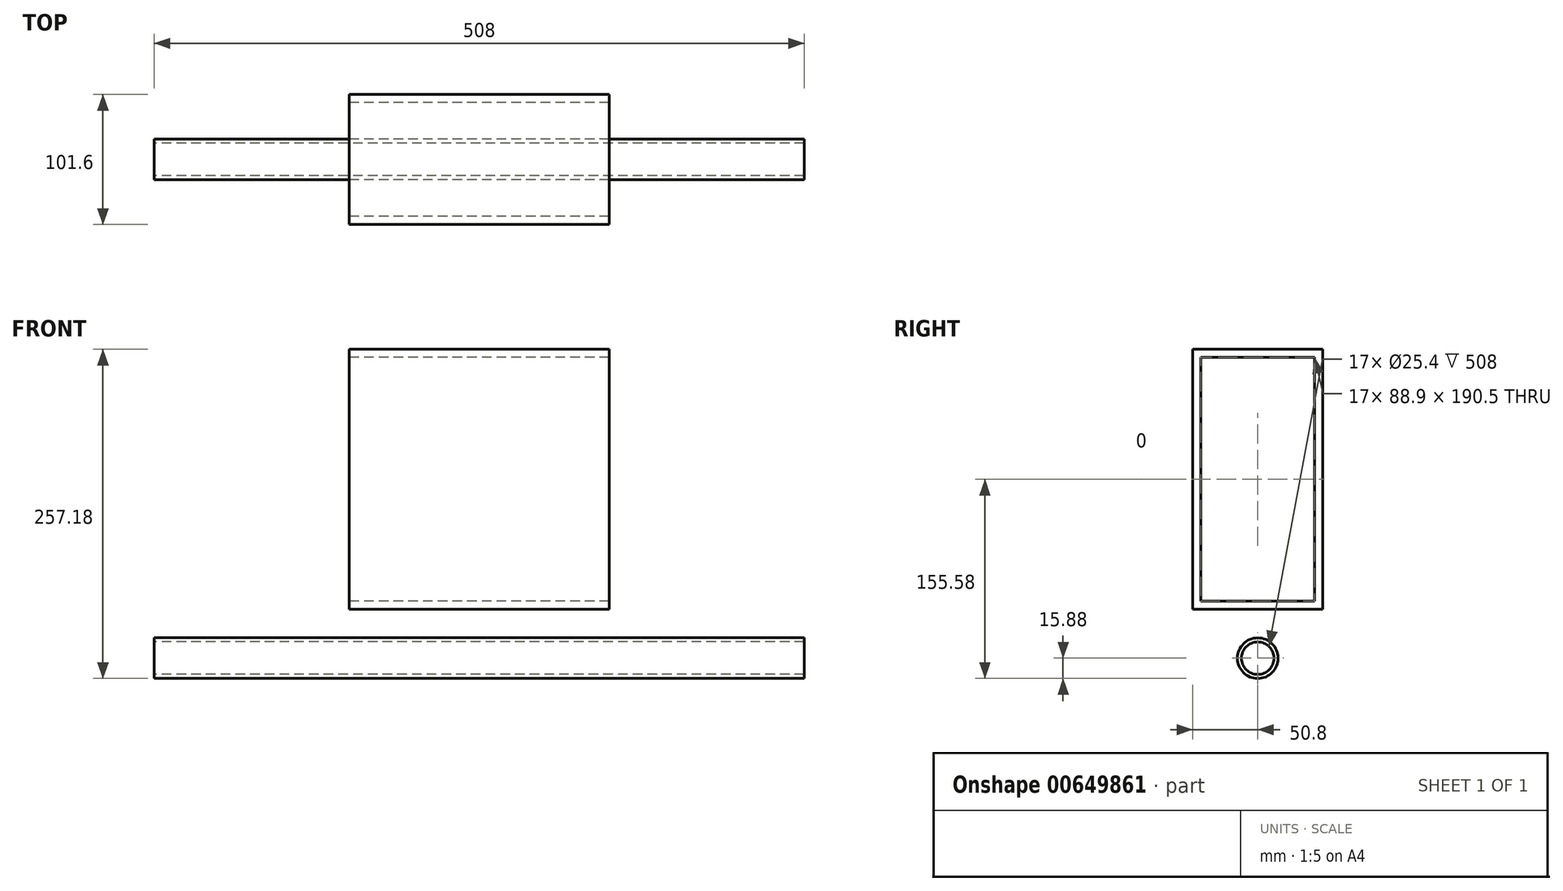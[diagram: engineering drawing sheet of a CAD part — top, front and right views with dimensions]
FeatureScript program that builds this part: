
annotation { "Feature Type Name" : "Feature", "Feature Type Description" : "" }
export const myFeature = defineFeature(function(context is Context, id is Id, definition is map)
    precondition{}
    {
        {
            var Q0;
            Q0=qCreatedBy(makeId("Right.planeOp"),FACE);
            var sketch = newSketch(context, id + "F0", { "sketchPlane" : qUnion([Q0])});
            skCircle(sketch, "E0", {"center": v(0, 0) * mm, "radius": 15.88 * mm});
            skCircle(sketch, "E1", {"center": v(0, 0) * mm, "radius": 12.7 * mm});
            skSolve(sketch);
        }
        {
            var Q0;
            Q0 = qSketchRegion(id + "F0", true);
            extrude(context, id + "F1", {"entities" : qUnion([Q0]), "depth" : 254 * mm, "offsetDistance" : 25.4 * mm, "hasSecondDirection" : true, "secondDirectionOppositeDirection" : true, "secondDirectionDepth" : 254 * mm});
        }
        {
            var Q0;
            Q0=qCreatedBy(makeId("Right.planeOp"),FACE);
            var sketch = newSketch(context, id + "F2", { "sketchPlane" : qUnion([Q0])});
            skLineSegment(sketch, "E2.bottom", {"start": v(-50.8, 241.3) * mm, "end": v(50.8, 241.3) * mm});
            skLineSegment(sketch, "E2.top", {"start": v(-50.8, 38.1) * mm, "end": v(50.8, 38.1) * mm});
            skLineSegment(sketch, "E2.left", {"start": v(-50.8, 241.3) * mm, "end": v(-50.8, 38.1) * mm});
            skLineSegment(sketch, "E2.right", {"start": v(50.8, 241.3) * mm, "end": v(50.8, 38.1) * mm});
            skLineSegment(sketch, "E3.0", {"start": v(-44.45, 234.95) * mm, "end": v(44.45, 234.95) * mm});
            skLineSegment(sketch, "E3.1", {"start": v(-44.45, 234.95) * mm, "end": v(-44.45, 44.45) * mm});
            skLineSegment(sketch, "E3.2", {"start": v(-44.45, 44.45) * mm, "end": v(44.45, 44.45) * mm});
            skLineSegment(sketch, "E3.3", {"start": v(44.45, 234.95) * mm, "end": v(44.45, 44.45) * mm});
            skSolve(sketch);
        }
        {
            var Q0;
            Q0=makeQuery(id+"F2.imprint","IMPRINT",FACE,{"disambiguationData":[TD([[makeQuery(id+"F2.imprint","IMPRINT",EDGE,{"derivedFrom":sQuery(id+"F2.wireOp",EDGE,"E2.bottom")}),-1.0]])]});
            extrude(context, id + "F3", {"entities" : qUnion([Q0]), "depth" : 101.6 * mm, "offsetDistance" : 25.4 * mm, "hasSecondDirection" : true, "secondDirectionOppositeDirection" : true, "secondDirectionDepth" : 101.6 * mm});
        }
        {
            var Q0;
            Q0=qCreatedBy(makeId("Front.planeOp"),FACE);
            var sketch = newSketch(context, id + "F4", { "sketchPlane" : qUnion([Q0])});
            skLineSegment(sketch, "E4.bottom", {"start": v(-101.6, 38.1) * mm, "end": v(101.6, 38.1) * mm});
            skLineSegment(sketch, "E4.top", {"start": v(-101.6, 0) * mm, "end": v(101.6, 0) * mm});
            skLineSegment(sketch, "E4.left", {"start": v(-101.6, 38.1) * mm, "end": v(-101.6, 0) * mm});
            skLineSegment(sketch, "E4.right", {"start": v(101.6, 38.1) * mm, "end": v(101.6, 0) * mm});
            skLineSegment(sketch, "E5.0", {"start": v(-95.25, 31.75) * mm, "end": v(-95.25, 0) * mm});
            skLineSegment(sketch, "E5.1", {"start": v(-95.25, 31.75) * mm, "end": v(95.25, 31.75) * mm});
            skLineSegment(sketch, "E5.2", {"start": v(95.25, 31.75) * mm, "end": v(95.25, 0) * mm});
            skSolve(sketch);
        }
        {
            var Q0;
            Q0=makeQuery(id+"F4.imprint","IMPRINT",FACE,{"disambiguationData":[TD([[makeQuery(id+"F4.imprint","IMPRINT",EDGE,{"derivedFrom":sQuery(id+"F4.wireOp",EDGE,"E4.bottom")}),-1.0]])]});
            extrude(context, id + "F5", {"entities" : qUnion([Q0]), "depth" : 63.5 * mm, "offsetDistance" : 25.4 * mm, "hasSecondDirection" : true, "secondDirectionOppositeDirection" : true, "secondDirectionDepth" : 63.5 * mm});
        }
        {
            var Q0;
            Q0=makeQuery(id+"F1.opExtrude","SWEPT_BODY",BODY,{"disambiguationData":[OSD([sQuery(id+"F0.wireOp",EDGE,"E0"),sQuery(id+"F0.wireOp",EDGE,"E1")])]});
            var Q1;
            Q1=makeQuery(id+"F5.opExtrude","SWEPT_BODY",BODY,{"disambiguationData":[OSD([sQuery(id+"F4.wireOp",EDGE,"E4.bottom"),sQuery(id+"F4.wireOp",EDGE,"E4.top"),sQuery(id+"F4.wireOp",EDGE,"E4.left"),sQuery(id+"F4.wireOp",EDGE,"E4.right"),sQuery(id+"F4.wireOp",EDGE,"E5.0"),sQuery(id+"F4.wireOp",EDGE,"E5.1"),sQuery(id+"F4.wireOp",EDGE,"E5.2")])]});
            booleanBodies(context, id + "F6", {"operationType" : BooleanOperationType.SUBTRACTION, "tools" : qUnion([Q0]), "targets" : qUnion([Q1]), "keepTools" : true});
        }
        {
            var Q0;
            Q0=makeQuery(id+"F6.opBoolean","SPLIT",BODY,{"disambiguationData":[OD(2.0)],"derivedFrom":makeQuery(id+"F5.opExtrude","SWEPT_BODY",BODY,{"disambiguationData":[OSD([sQuery(id+"F4.wireOp",EDGE,"E4.bottom"),sQuery(id+"F4.wireOp",EDGE,"E4.top"),sQuery(id+"F4.wireOp",EDGE,"E4.left"),sQuery(id+"F4.wireOp",EDGE,"E4.right"),sQuery(id+"F4.wireOp",EDGE,"E5.0"),sQuery(id+"F4.wireOp",EDGE,"E5.1"),sQuery(id+"F4.wireOp",EDGE,"E5.2")])]})});
            var Q1;
            Q1=makeQuery(id+"F6.opBoolean","SPLIT",BODY,{"disambiguationData":[OD(1.0)],"derivedFrom":makeQuery(id+"F5.opExtrude","SWEPT_BODY",BODY,{"disambiguationData":[OSD([sQuery(id+"F4.wireOp",EDGE,"E4.bottom"),sQuery(id+"F4.wireOp",EDGE,"E4.top"),sQuery(id+"F4.wireOp",EDGE,"E4.left"),sQuery(id+"F4.wireOp",EDGE,"E4.right"),sQuery(id+"F4.wireOp",EDGE,"E5.0"),sQuery(id+"F4.wireOp",EDGE,"E5.1"),sQuery(id+"F4.wireOp",EDGE,"E5.2")])]})});
            deleteBodies(context, id + "F7", {"entities" : qUnion([Q0, Q1])});
        }
    });
